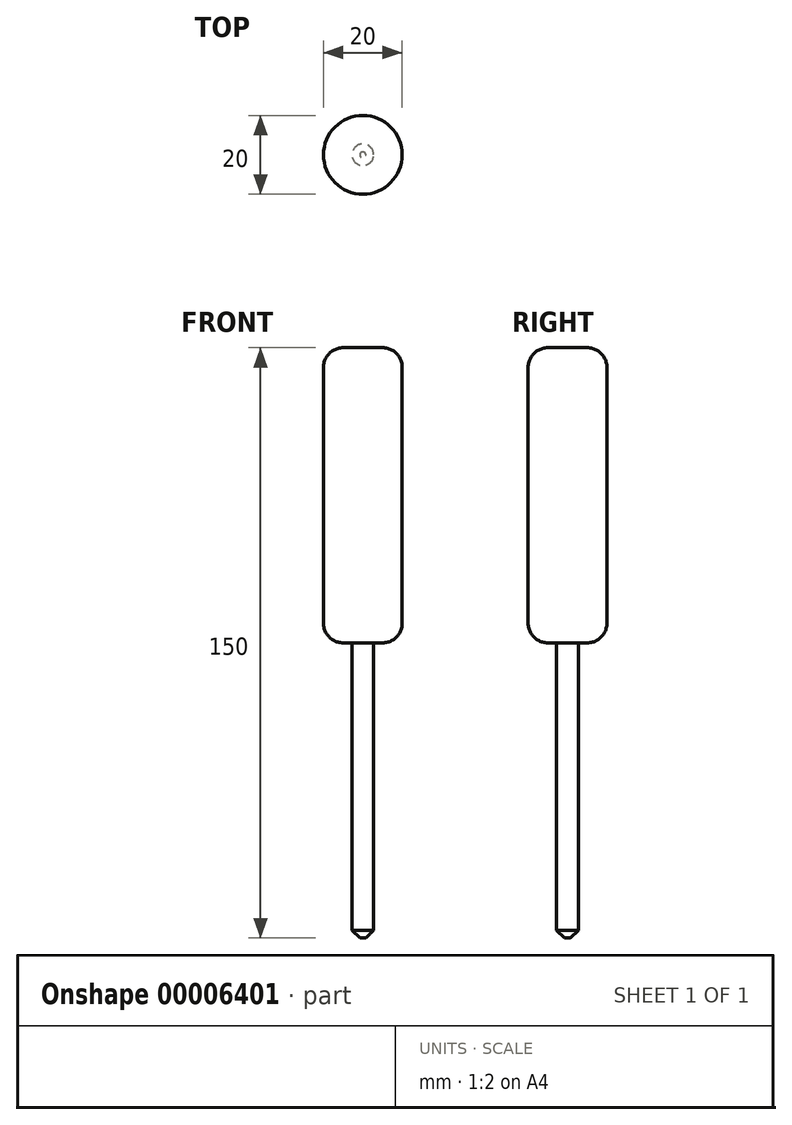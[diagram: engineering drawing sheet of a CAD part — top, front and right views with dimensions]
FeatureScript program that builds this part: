
annotation { "Feature Type Name" : "Feature", "Feature Type Description" : "" }
export const myFeature = defineFeature(function(context is Context, id is Id, definition is map)
    precondition{}
    {
        {
            var Q0;
            Q0=qCreatedBy(makeId("Front.planeOp"),FACE);
            var sketch = newSketch(context, id + "F0", { "sketchPlane" : qUnion([Q0])});
            skLineSegment(sketch, "E0.bottom", {"start": v(-10, 75) * mm, "end": v(0, 75) * mm});
            skLineSegment(sketch, "E0.top", {"start": v(-10, 0) * mm, "end": v(0, 0) * mm});
            skLineSegment(sketch, "E0.left", {"start": v(-10, 75) * mm, "end": v(-10, 0) * mm});
            skLineSegment(sketch, "E0.right", {"start": v(0, 75) * mm, "end": v(0, 0) * mm});
            skLineSegment(sketch, "E1.bottom", {"start": v(0, 0) * mm, "end": v(-2.75, 0) * mm});
            skLineSegment(sketch, "E1.top", {"start": v(0, -75) * mm, "end": v(-2.75, -75) * mm});
            skLineSegment(sketch, "E1.left", {"start": v(0, 0) * mm, "end": v(0, -75) * mm});
            skLineSegment(sketch, "E1.right", {"start": v(-2.75, 0) * mm, "end": v(-2.75, -75) * mm});
            skSolve(sketch);
        }
        {
            var Q0;
            Q0 = qSketchRegion(id + "F0", true);
            var Q1;
            Q1=sQuery(id+"F0.wireOp",EDGE,"E0.right");
            revolve(context, id + "F1", {"entities" : qUnion([Q0]), "axis" : qUnion([Q1]), "revolveType" : RevolveType.FULL});
        }
        {
            var Q0;
            Q0=makeQuery(id+"F1.opRevolve","SWEPT_FACE",FACE,{"disambiguationData":[OSD([sQuery(id+"F0.wireOp",EDGE,"E0.left")])]});
            fillet(context, id + "F2", {"entities" : qUnion([Q0]), "radius" : 5 * mm, "tangentPropagation" : true, "allowEdgeOverflow" : false});
        }
        {
            var Q0;
            Q0=makeQuery(id+"F1.opRevolve","SWEPT_EDGE",EDGE,{"disambiguationData":[OSD([sQuery(id+"F0.wireOp",EDGE,"E1.top"),sQuery(id+"F0.wireOp",EDGE,"E1.right")])]});
            chamfer(context, id + "F3", {"entities" : qUnion([Q0]), "width" : 2 * mm, "tangentPropagation" : true});
        }
    });
